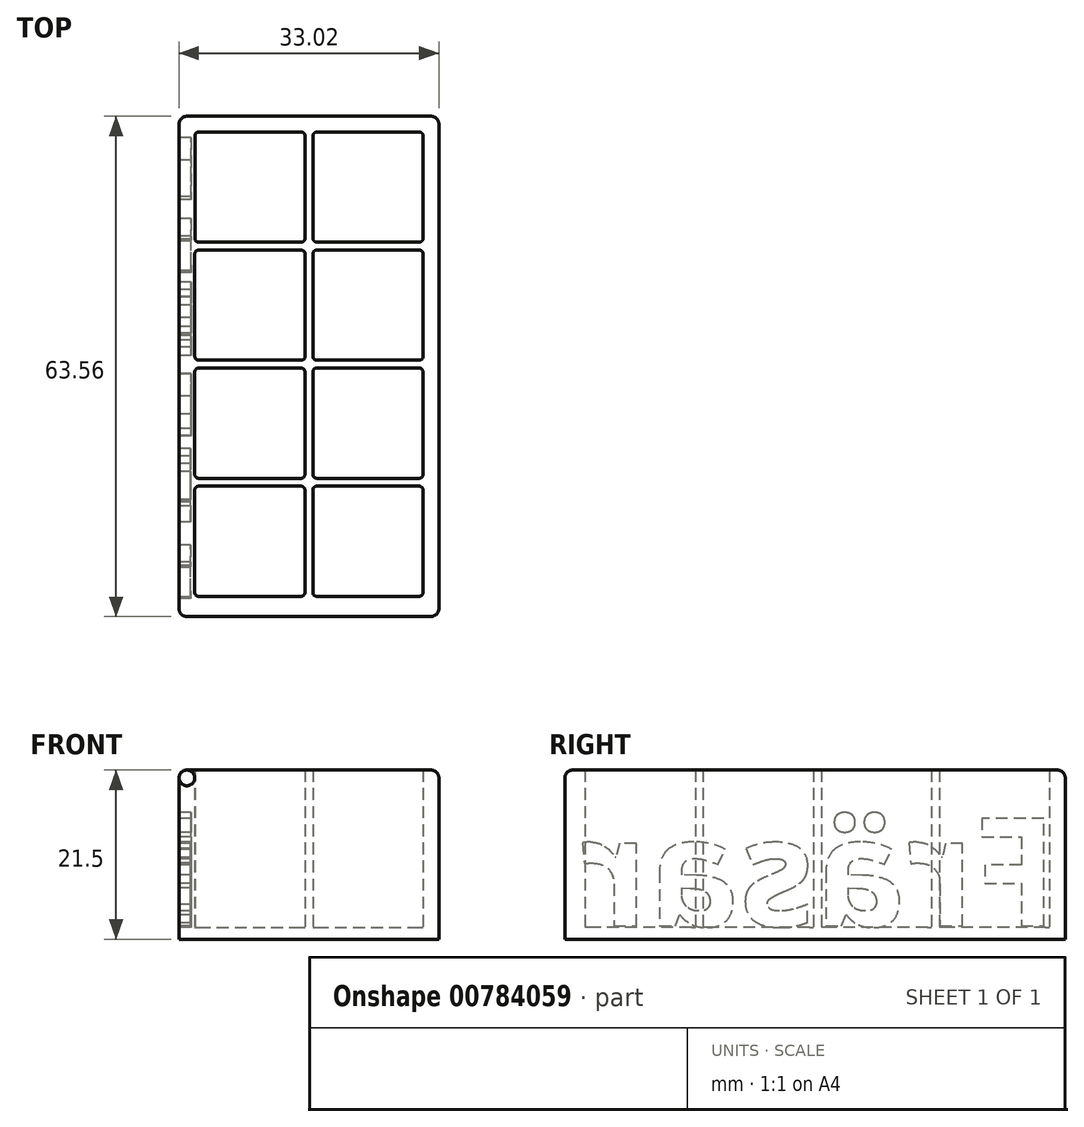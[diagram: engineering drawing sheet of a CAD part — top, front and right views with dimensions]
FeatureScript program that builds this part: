
annotation { "Feature Type Name" : "Feature", "Feature Type Description" : "" }
export const myFeature = defineFeature(function(context is Context, id is Id, definition is map)
    precondition{}
    {
        {
            var Q0;
            Q0=qCreatedBy(makeId("Top.planeOp"),FACE);
            var sketch = newSketch(context, id + "F0", { "sketchPlane" : qUnion([Q0])});
            skLineSegment(sketch, "E0.bottom", {"start": v(-10.2, 14) * mm, "end": v(3.8, 14) * mm});
            skLineSegment(sketch, "E0.top", {"start": v(-10.2, 0) * mm, "end": v(3.8, 0) * mm});
            skLineSegment(sketch, "E0.left", {"start": v(-10.2, 14) * mm, "end": v(-10.2, 0) * mm});
            skLineSegment(sketch, "E0.right", {"start": v(3.8, 14) * mm, "end": v(3.8, 0) * mm});
            skLineSegment(sketch, "E1.0.1.0", {"start": v(-10.2, -1) * mm, "end": v(3.8, -1) * mm});
            skLineSegment(sketch, "E1.0.1.1", {"start": v(-10.2, -1) * mm, "end": v(-10.2, -15) * mm});
            skLineSegment(sketch, "E1.0.1.2", {"start": v(3.8, -1) * mm, "end": v(3.8, -15) * mm});
            skLineSegment(sketch, "E1.0.1.3", {"start": v(-10.2, -15) * mm, "end": v(3.8, -15) * mm});
            skLineSegment(sketch, "E1.0.2.0", {"start": v(-10.2, -16) * mm, "end": v(3.8, -16) * mm});
            skLineSegment(sketch, "E1.0.2.1", {"start": v(-10.2, -16) * mm, "end": v(-10.2, -30) * mm});
            skLineSegment(sketch, "E1.0.2.2", {"start": v(3.8, -16) * mm, "end": v(3.8, -30) * mm});
            skLineSegment(sketch, "E1.0.2.3", {"start": v(-10.2, -30) * mm, "end": v(3.8, -30) * mm});
            skLineSegment(sketch, "E1.0.3.0", {"start": v(-10.2, -31) * mm, "end": v(3.8, -31) * mm});
            skLineSegment(sketch, "E1.0.3.1", {"start": v(-10.2, -31) * mm, "end": v(-10.2, -45) * mm});
            skLineSegment(sketch, "E1.0.3.2", {"start": v(3.8, -31) * mm, "end": v(3.8, -45) * mm});
            skLineSegment(sketch, "E1.0.3.3", {"start": v(-10.2, -45) * mm, "end": v(3.8, -45) * mm});
            skLineSegment(sketch, "E1.1.0.0", {"start": v(4.8, 14) * mm, "end": v(18.8, 14) * mm});
            skLineSegment(sketch, "E1.1.0.1", {"start": v(4.8, 14) * mm, "end": v(4.8, 0) * mm});
            skLineSegment(sketch, "E1.1.0.2", {"start": v(18.8, 14) * mm, "end": v(18.8, 0) * mm});
            skLineSegment(sketch, "E1.1.0.3", {"start": v(4.8, 0) * mm, "end": v(18.8, 0) * mm});
            skLineSegment(sketch, "E1.1.1.0", {"start": v(4.8, -1) * mm, "end": v(18.8, -1) * mm});
            skLineSegment(sketch, "E1.1.1.1", {"start": v(4.8, -1) * mm, "end": v(4.8, -15) * mm});
            skLineSegment(sketch, "E1.1.1.2", {"start": v(18.8, -1) * mm, "end": v(18.8, -15) * mm});
            skLineSegment(sketch, "E1.1.1.3", {"start": v(4.8, -15) * mm, "end": v(18.8, -15) * mm});
            skLineSegment(sketch, "E1.1.2.0", {"start": v(4.8, -16) * mm, "end": v(18.8, -16) * mm});
            skLineSegment(sketch, "E1.1.2.1", {"start": v(4.8, -16) * mm, "end": v(4.8, -30) * mm});
            skLineSegment(sketch, "E1.1.2.2", {"start": v(18.8, -16) * mm, "end": v(18.8, -30) * mm});
            skLineSegment(sketch, "E1.1.2.3", {"start": v(4.8, -30) * mm, "end": v(18.8, -30) * mm});
            skLineSegment(sketch, "E1.1.3.0", {"start": v(4.8, -31) * mm, "end": v(18.8, -31) * mm});
            skLineSegment(sketch, "E1.1.3.1", {"start": v(4.8, -31) * mm, "end": v(4.8, -45) * mm});
            skLineSegment(sketch, "E1.1.3.2", {"start": v(18.8, -31) * mm, "end": v(18.8, -45) * mm});
            skLineSegment(sketch, "E1.1.3.3", {"start": v(4.8, -45) * mm, "end": v(18.8, -45) * mm});
            skLineSegment(sketch, "E1.direction1", {"start": v(-10.2, 14) * mm, "end": v(4.8, 14) * mm, "construction": true});
            skLineSegment(sketch, "E1.direction2", {"start": v(-10.2, 14) * mm, "end": v(-10.2, -1) * mm, "construction": true});
            skPoint(sketch, "E2.bottom.start.orphan", {"position": v(-10.2, -46) * mm});
            skSolve(sketch);
        }
        {
            var Q0;
            Q0=qCreatedBy(makeId("Top.planeOp"),FACE);
            var sketch = newSketch(context, id + "F1", { "sketchPlane" : qUnion([Q0])});
            skLineSegment(sketch, "E3", {"start": v(-10.2, 14) * mm, "end": v(18.8, 14) * mm});
            skLineSegment(sketch, "E4", {"start": v(18.8, 14) * mm, "end": v(18.8, -45.05) * mm});
            skLineSegment(sketch, "E5", {"start": v(18.8, -45.05) * mm, "end": v(-10.2, -45.05) * mm});
            skLineSegment(sketch, "E6", {"start": v(-10.2, -45.05) * mm, "end": v(-10.2, 14) * mm});
            skLineSegment(sketch, "E7.0", {"start": v(20.8, 16) * mm, "end": v(20.8, -47.56) * mm});
            skLineSegment(sketch, "E7.2", {"start": v(20.9, -47.56) * mm, "end": v(-12.2, -47.56) * mm});
            skLineSegment(sketch, "E7.4", {"start": v(-12.2, -47.56) * mm, "end": v(-12.2, 16) * mm});
            skLineSegment(sketch, "E7.5", {"start": v(-12.2, 16) * mm, "end": v(20.8, 16) * mm});
            skSolve(sketch);
        }
        {
            var Q0;
            Q0=makeQuery(id+"F1.imprint","IMPRINT",FACE,{"disambiguationData":[TD([[makeQuery(id+"F1.imprint","IMPRINT",EDGE,{"derivedFrom":sQuery(id+"F1.wireOp",EDGE,"E3")}),1.0]])]});
            var Q1;
            Q1=makeQuery(id+"F1.imprint","IMPRINT",FACE,{"disambiguationData":[TD([[makeQuery(id+"F1.imprint","IMPRINT",EDGE,{"derivedFrom":sQuery(id+"F1.wireOp",EDGE,"E3")}),-1.0]])]});
            extrude(context, id + "F2", {"entities" : qUnion([Q0, Q1]), "depth" : 20 * mm, "offsetDistance" : 25 * mm, "hasSecondDirection" : true, "secondDirectionOppositeDirection" : true, "secondDirectionDepth" : 1.5 * mm});
        }
        {
            var Q0;
            Q0=makeQuery(id+"F0.imprint","IMPRINT",FACE,{"disambiguationData":[TD([[makeQuery(id+"F0.imprint","IMPRINT",EDGE,{"derivedFrom":sQuery(id+"F0.wireOp",EDGE,"E0.bottom")}),-1.0]])]});
            var Q1;
            Q1=makeQuery(id+"F0.imprint","IMPRINT",FACE,{"disambiguationData":[TD([[makeQuery(id+"F0.imprint","IMPRINT",EDGE,{"derivedFrom":sQuery(id+"F0.wireOp",EDGE,"E1.1.0.0")}),-1.0]])]});
            var Q2;
            Q2=makeQuery(id+"F0.imprint","IMPRINT",FACE,{"disambiguationData":[TD([[makeQuery(id+"F0.imprint","IMPRINT",EDGE,{"derivedFrom":sQuery(id+"F0.wireOp",EDGE,"E1.0.1.0")}),-1.0]])]});
            var Q3;
            Q3=makeQuery(id+"F0.imprint","IMPRINT",FACE,{"disambiguationData":[TD([[makeQuery(id+"F0.imprint","IMPRINT",EDGE,{"derivedFrom":sQuery(id+"F0.wireOp",EDGE,"E1.1.1.0")}),-1.0]])]});
            var Q4;
            Q4=makeQuery(id+"F0.imprint","IMPRINT",FACE,{"disambiguationData":[TD([[makeQuery(id+"F0.imprint","IMPRINT",EDGE,{"derivedFrom":sQuery(id+"F0.wireOp",EDGE,"E1.0.2.0")}),-1.0]])]});
            var Q5;
            Q5=makeQuery(id+"F0.imprint","IMPRINT",FACE,{"disambiguationData":[TD([[makeQuery(id+"F0.imprint","IMPRINT",EDGE,{"derivedFrom":sQuery(id+"F0.wireOp",EDGE,"E1.1.2.0")}),-1.0]])]});
            var Q6;
            Q6=makeQuery(id+"F0.imprint","IMPRINT",FACE,{"disambiguationData":[TD([[makeQuery(id+"F0.imprint","IMPRINT",EDGE,{"derivedFrom":sQuery(id+"F0.wireOp",EDGE,"E1.0.3.0")}),-1.0]])]});
            var Q7;
            Q7=makeQuery(id+"F0.imprint","IMPRINT",FACE,{"disambiguationData":[TD([[makeQuery(id+"F0.imprint","IMPRINT",EDGE,{"derivedFrom":sQuery(id+"F0.wireOp",EDGE,"E1.1.3.0")}),-1.0]])]});
            var Q8;
            Q8=makeQuery(id+"F0.imprint","IMPRINT",FACE,{"disambiguationData":[TD([[makeQuery(id+"F0.imprint","IMPRINT",EDGE,{"derivedFrom":sQuery(id+"F0.wireOp",EDGE,"E2.bottom")}),-1.0]])]});
            var Q9;
            Q9=makeQuery(id+"F0.imprint","IMPRINT",FACE,{"disambiguationData":[TD([[makeQuery(id+"F0.imprint","IMPRINT",EDGE,{"derivedFrom":sQuery(id+"F0.wireOp",EDGE,"f9a36279-b497-429b-bdca-f29c6110149f.1.0.0")}),-1.0]])]});
            var Q10;
            Q10=makeQuery(id+"F2.opExtrude","CAP_FACE",FACE,{"disambiguationData":[OSD([sQuery(id+"F1.wireOp",EDGE,"E7.0"),sQuery(id+"F1.wireOp",EDGE,"E7.1"),sQuery(id+"F1.wireOp",EDGE,"E7.2"),sQuery(id+"F1.wireOp",EDGE,"E7.3"),sQuery(id+"F1.wireOp",EDGE,"E7.4"),sQuery(id+"F1.wireOp",EDGE,"E7.5")])],"isStart":false});
            extrude(context, id + "F3", {"entities" : qUnion([Q0, Q1, Q2, Q3, Q4, Q5, Q6, Q7, Q8, Q9]), "operationType" : NewBodyOperationType.REMOVE, "endBound" : BoundingType.UP_TO_SURFACE, "depth" : 25 * mm, "endBoundEntityFace" : qUnion([Q10]), "offsetDistance" : 25 * mm});
        }
        {
            var Q0;
            Q0=makeQuery(id+"F2.opExtrude","CAP_EDGE",EDGE,{"disambiguationData":[OSD([sQuery(id+"F1.wireOp",EDGE,"E7.0")])],"isStart":false});
            var Q1;
            Q1=makeQuery(id+"F2.opExtrude","CAP_EDGE",EDGE,{"disambiguationData":[OSD([sQuery(id+"F1.wireOp",EDGE,"E7.3")])],"isStart":false});
            var Q2;
            Q2=makeQuery(id+"F2.opExtrude","CAP_EDGE",EDGE,{"disambiguationData":[OSD([sQuery(id+"F1.wireOp",EDGE,"E7.1")])],"isStart":false});
            var Q3;
            Q3=makeQuery(id+"F2.opExtrude","CAP_EDGE",EDGE,{"disambiguationData":[OSD([sQuery(id+"F1.wireOp",EDGE,"E7.4")])],"isStart":false});
            var Q4;
            Q4=makeQuery(id+"F2.opExtrude","SWEPT_EDGE",EDGE,{"disambiguationData":[OSD([sQuery(id+"F1.wireOp",EDGE,"E7.1"),sQuery(id+"F1.wireOp",EDGE,"E7.2")])]});
            var Q5;
            Q5=makeQuery(id+"F2.opExtrude","SWEPT_EDGE",EDGE,{"disambiguationData":[OSD([sQuery(id+"F1.wireOp",EDGE,"E7.1"),sQuery(id+"F1.wireOp",EDGE,"E7.3")])]});
            var Q6;
            Q6=makeQuery(id+"F2.opExtrude","SWEPT_EDGE",EDGE,{"disambiguationData":[OSD([sQuery(id+"F1.wireOp",EDGE,"E7.0"),sQuery(id+"F1.wireOp",EDGE,"E7.5")])]});
            var Q7;
            Q7=makeQuery(id+"F2.opExtrude","CAP_EDGE",EDGE,{"disambiguationData":[OSD([sQuery(id+"F1.wireOp",EDGE,"E7.5")])],"isStart":false});
            var Q8;
            Q8=makeQuery(id+"F2.opExtrude","SWEPT_EDGE",EDGE,{"disambiguationData":[OSD([sQuery(id+"F1.wireOp",EDGE,"E7.4"),sQuery(id+"F1.wireOp",EDGE,"E7.5")])]});
            var Q9;
            Q9=makeQuery(id+"F2.opExtrude","SWEPT_EDGE",EDGE,{"disambiguationData":[OSD([sQuery(id+"F1.wireOp",EDGE,"E7.0"),sQuery(id+"F1.wireOp",EDGE,"E7.3")])]});
            var Q10;
            Q10=makeQuery(id+"F2.opExtrude","CAP_EDGE",EDGE,{"disambiguationData":[OSD([sQuery(id+"F1.wireOp",EDGE,"E7.2")])],"isStart":false});
            var Q11;
            Q11=makeQuery(id+"F2.opExtrude","SWEPT_EDGE",EDGE,{"disambiguationData":[OSD([sQuery(id+"F1.wireOp",EDGE,"E7.2"),sQuery(id+"F1.wireOp",EDGE,"E7.4")])]});
            fillet(context, id + "F4", {"entities" : qUnion([Q0, Q1, Q2, Q3, Q4, Q5, Q6, Q7, Q8, Q9, Q10, Q11]), "radius" : 1 * mm, "allowEdgeOverflow" : false});
        }
        {
            var Q0;
            Q0=makeQuery(id+"F3.boolean.opBoolean","COPY",EDGE,{"derivedFrom":makeQuery(id+"F3.opExtrude","SWEPT_EDGE",EDGE,{"disambiguationData":[OSD([sQuery(id+"F0.wireOp",EDGE,"E1.1.0.0"),sQuery(id+"F0.wireOp",EDGE,"E1.1.0.2")])]})});
            var Q1;
            Q1=makeQuery(id+"F3.boolean.opBoolean","COPY",EDGE,{"derivedFrom":makeQuery(id+"F3.opExtrude","SWEPT_EDGE",EDGE,{"disambiguationData":[OSD([sQuery(id+"F0.wireOp",EDGE,"E1.1.1.0"),sQuery(id+"F0.wireOp",EDGE,"E1.1.1.2")])]})});
            var Q2;
            Q2=makeQuery(id+"F3.boolean.opBoolean","COPY",EDGE,{"derivedFrom":makeQuery(id+"F3.opExtrude","SWEPT_EDGE",EDGE,{"disambiguationData":[OSD([sQuery(id+"F0.wireOp",EDGE,"E1.1.2.0"),sQuery(id+"F0.wireOp",EDGE,"E1.1.2.2")])]})});
            var Q3;
            Q3=makeQuery(id+"F3.boolean.opBoolean","COPY",EDGE,{"derivedFrom":makeQuery(id+"F3.opExtrude","SWEPT_EDGE",EDGE,{"disambiguationData":[OSD([sQuery(id+"F0.wireOp",EDGE,"E1.1.3.0"),sQuery(id+"F0.wireOp",EDGE,"E1.1.3.2")])]})});
            var Q4;
            Q4=makeQuery(id+"F3.boolean.opBoolean","COPY",EDGE,{"derivedFrom":makeQuery(id+"F3.opExtrude","SWEPT_EDGE",EDGE,{"disambiguationData":[OSD([sQuery(id+"F0.wireOp",EDGE,"f9a36279-b497-429b-bdca-f29c6110149f.1.0.0"),sQuery(id+"F0.wireOp",EDGE,"f9a36279-b497-429b-bdca-f29c6110149f.1.0.1")])]})});
            var Q5;
            Q5=makeQuery(id+"F3.boolean.opBoolean","COPY",EDGE,{"derivedFrom":makeQuery(id+"F3.opExtrude","SWEPT_EDGE",EDGE,{"disambiguationData":[OSD([sQuery(id+"F0.wireOp",EDGE,"E0.bottom"),sQuery(id+"F0.wireOp",EDGE,"E0.right")])]})});
            var Q6;
            Q6=makeQuery(id+"F3.boolean.opBoolean","COPY",EDGE,{"derivedFrom":makeQuery(id+"F3.opExtrude","SWEPT_EDGE",EDGE,{"disambiguationData":[OSD([sQuery(id+"F0.wireOp",EDGE,"E1.0.1.0"),sQuery(id+"F0.wireOp",EDGE,"E1.0.1.2")])]})});
            var Q7;
            Q7=makeQuery(id+"F3.boolean.opBoolean","COPY",EDGE,{"derivedFrom":makeQuery(id+"F3.opExtrude","SWEPT_EDGE",EDGE,{"disambiguationData":[OSD([sQuery(id+"F0.wireOp",EDGE,"E1.0.2.0"),sQuery(id+"F0.wireOp",EDGE,"E1.0.2.2")])]})});
            var Q8;
            Q8=makeQuery(id+"F3.boolean.opBoolean","COPY",EDGE,{"derivedFrom":makeQuery(id+"F3.opExtrude","SWEPT_EDGE",EDGE,{"disambiguationData":[OSD([sQuery(id+"F0.wireOp",EDGE,"E1.0.3.0"),sQuery(id+"F0.wireOp",EDGE,"E1.0.3.2")])]})});
            var Q9;
            Q9=makeQuery(id+"F3.boolean.opBoolean","COPY",EDGE,{"derivedFrom":makeQuery(id+"F3.opExtrude","SWEPT_EDGE",EDGE,{"disambiguationData":[OSD([sQuery(id+"F0.wireOp",EDGE,"E2.bottom"),sQuery(id+"F0.wireOp",EDGE,"E2.right")])]})});
            var Q10;
            Q10=makeQuery(id+"F3.boolean.opBoolean","COPY",EDGE,{"derivedFrom":makeQuery(id+"F3.opExtrude","SWEPT_EDGE",EDGE,{"disambiguationData":[OSD([sQuery(id+"F0.wireOp",EDGE,"E1.1.0.2"),sQuery(id+"F0.wireOp",EDGE,"E1.1.0.3")])]})});
            var Q11;
            Q11=makeQuery(id+"F3.boolean.opBoolean","COPY",EDGE,{"derivedFrom":makeQuery(id+"F3.opExtrude","SWEPT_EDGE",EDGE,{"disambiguationData":[OSD([sQuery(id+"F0.wireOp",EDGE,"E1.1.1.2"),sQuery(id+"F0.wireOp",EDGE,"E1.1.1.3")])]})});
            var Q12;
            Q12=makeQuery(id+"F3.boolean.opBoolean","COPY",EDGE,{"derivedFrom":makeQuery(id+"F3.opExtrude","SWEPT_EDGE",EDGE,{"disambiguationData":[OSD([sQuery(id+"F0.wireOp",EDGE,"E1.1.2.2"),sQuery(id+"F0.wireOp",EDGE,"E1.1.2.3")])]})});
            var Q13;
            Q13=makeQuery(id+"F3.boolean.opBoolean","COPY",EDGE,{"derivedFrom":makeQuery(id+"F3.opExtrude","SWEPT_EDGE",EDGE,{"disambiguationData":[OSD([sQuery(id+"F0.wireOp",EDGE,"E1.1.3.2"),sQuery(id+"F0.wireOp",EDGE,"E1.1.3.3")])]})});
            var Q14;
            Q14=makeQuery(id+"F3.boolean.opBoolean","COPY",EDGE,{"derivedFrom":makeQuery(id+"F3.opExtrude","SWEPT_EDGE",EDGE,{"disambiguationData":[OSD([sQuery(id+"F0.wireOp",EDGE,"f9a36279-b497-429b-bdca-f29c6110149f.1.0.0"),sQuery(id+"F0.wireOp",EDGE,"f9a36279-b497-429b-bdca-f29c6110149f.1.0.3")])]})});
            var Q15;
            Q15=makeQuery(id+"F3.boolean.opBoolean","COPY",EDGE,{"derivedFrom":makeQuery(id+"F3.opExtrude","SWEPT_EDGE",EDGE,{"disambiguationData":[OSD([sQuery(id+"F0.wireOp",EDGE,"E2.top"),sQuery(id+"F0.wireOp",EDGE,"E2.right")])]})});
            var Q16;
            Q16=makeQuery(id+"F3.boolean.opBoolean","COPY",EDGE,{"derivedFrom":makeQuery(id+"F3.opExtrude","SWEPT_EDGE",EDGE,{"disambiguationData":[OSD([sQuery(id+"F0.wireOp",EDGE,"E1.0.3.2"),sQuery(id+"F0.wireOp",EDGE,"E1.0.3.3")])]})});
            var Q17;
            Q17=makeQuery(id+"F3.boolean.opBoolean","COPY",EDGE,{"derivedFrom":makeQuery(id+"F3.opExtrude","SWEPT_EDGE",EDGE,{"disambiguationData":[OSD([sQuery(id+"F0.wireOp",EDGE,"E1.0.2.2"),sQuery(id+"F0.wireOp",EDGE,"E1.0.2.3")])]})});
            var Q18;
            Q18=makeQuery(id+"F3.boolean.opBoolean","COPY",EDGE,{"derivedFrom":makeQuery(id+"F3.opExtrude","SWEPT_EDGE",EDGE,{"disambiguationData":[OSD([sQuery(id+"F0.wireOp",EDGE,"E1.0.1.2"),sQuery(id+"F0.wireOp",EDGE,"E1.0.1.3")])]})});
            var Q19;
            Q19=makeQuery(id+"F3.boolean.opBoolean","COPY",EDGE,{"derivedFrom":makeQuery(id+"F3.opExtrude","SWEPT_EDGE",EDGE,{"disambiguationData":[OSD([sQuery(id+"F0.wireOp",EDGE,"E0.top"),sQuery(id+"F0.wireOp",EDGE,"E0.right")])]})});
            var Q20;
            Q20=makeQuery(id+"F3.boolean.opBoolean","COPY",EDGE,{"derivedFrom":makeQuery(id+"F3.opExtrude","SWEPT_EDGE",EDGE,{"disambiguationData":[OSD([sQuery(id+"F0.wireOp",EDGE,"E0.bottom"),sQuery(id+"F0.wireOp",EDGE,"E0.left")])]})});
            var Q21;
            Q21=makeQuery(id+"F3.boolean.opBoolean","COPY",EDGE,{"derivedFrom":makeQuery(id+"F3.opExtrude","SWEPT_EDGE",EDGE,{"disambiguationData":[OSD([sQuery(id+"F0.wireOp",EDGE,"E1.0.1.0"),sQuery(id+"F0.wireOp",EDGE,"E1.0.1.1")])]})});
            var Q22;
            Q22=makeQuery(id+"F3.boolean.opBoolean","COPY",EDGE,{"derivedFrom":makeQuery(id+"F3.opExtrude","SWEPT_EDGE",EDGE,{"disambiguationData":[OSD([sQuery(id+"F0.wireOp",EDGE,"E1.0.2.0"),sQuery(id+"F0.wireOp",EDGE,"E1.0.2.1")])]})});
            var Q23;
            Q23=makeQuery(id+"F3.boolean.opBoolean","COPY",EDGE,{"derivedFrom":makeQuery(id+"F3.opExtrude","SWEPT_EDGE",EDGE,{"disambiguationData":[OSD([sQuery(id+"F0.wireOp",EDGE,"E1.0.3.0"),sQuery(id+"F0.wireOp",EDGE,"E1.0.3.1")])]})});
            var Q24;
            Q24=makeQuery(id+"F3.boolean.opBoolean","COPY",EDGE,{"derivedFrom":makeQuery(id+"F3.opExtrude","SWEPT_EDGE",EDGE,{"disambiguationData":[OSD([sQuery(id+"F0.wireOp",EDGE,"E2.bottom"),sQuery(id+"F0.wireOp",EDGE,"E2.left")])]})});
            var Q25;
            Q25=makeQuery(id+"F3.boolean.opBoolean","COPY",EDGE,{"derivedFrom":makeQuery(id+"F3.opExtrude","SWEPT_EDGE",EDGE,{"disambiguationData":[OSD([sQuery(id+"F0.wireOp",EDGE,"E2.top"),sQuery(id+"F0.wireOp",EDGE,"E2.left")])]})});
            var Q26;
            Q26=makeQuery(id+"F3.boolean.opBoolean","COPY",EDGE,{"derivedFrom":makeQuery(id+"F3.opExtrude","SWEPT_EDGE",EDGE,{"disambiguationData":[OSD([sQuery(id+"F0.wireOp",EDGE,"E1.0.1.1"),sQuery(id+"F0.wireOp",EDGE,"E1.0.1.3")])]})});
            var Q27;
            Q27=makeQuery(id+"F3.boolean.opBoolean","COPY",EDGE,{"derivedFrom":makeQuery(id+"F3.opExtrude","SWEPT_EDGE",EDGE,{"disambiguationData":[OSD([sQuery(id+"F0.wireOp",EDGE,"E0.top"),sQuery(id+"F0.wireOp",EDGE,"E0.left")])]})});
            var Q28;
            Q28=makeQuery(id+"F3.boolean.opBoolean","COPY",EDGE,{"derivedFrom":makeQuery(id+"F3.opExtrude","SWEPT_EDGE",EDGE,{"disambiguationData":[OSD([sQuery(id+"F0.wireOp",EDGE,"E1.1.0.0"),sQuery(id+"F0.wireOp",EDGE,"E1.1.0.1")])]})});
            var Q29;
            Q29=makeQuery(id+"F3.boolean.opBoolean","COPY",EDGE,{"derivedFrom":makeQuery(id+"F3.opExtrude","SWEPT_EDGE",EDGE,{"disambiguationData":[OSD([sQuery(id+"F0.wireOp",EDGE,"E1.1.0.1"),sQuery(id+"F0.wireOp",EDGE,"E1.1.0.3")])]})});
            var Q30;
            Q30=makeQuery(id+"F3.boolean.opBoolean","COPY",EDGE,{"derivedFrom":makeQuery(id+"F3.opExtrude","SWEPT_EDGE",EDGE,{"disambiguationData":[OSD([sQuery(id+"F0.wireOp",EDGE,"E1.1.1.0"),sQuery(id+"F0.wireOp",EDGE,"E1.1.1.1")])]})});
            var Q31;
            Q31=makeQuery(id+"F3.boolean.opBoolean","COPY",EDGE,{"derivedFrom":makeQuery(id+"F3.opExtrude","SWEPT_EDGE",EDGE,{"disambiguationData":[OSD([sQuery(id+"F0.wireOp",EDGE,"E1.1.1.1"),sQuery(id+"F0.wireOp",EDGE,"E1.1.1.3")])]})});
            var Q32;
            Q32=makeQuery(id+"F3.boolean.opBoolean","COPY",EDGE,{"derivedFrom":makeQuery(id+"F3.opExtrude","SWEPT_EDGE",EDGE,{"disambiguationData":[OSD([sQuery(id+"F0.wireOp",EDGE,"E1.1.2.0"),sQuery(id+"F0.wireOp",EDGE,"E1.1.2.1")])]})});
            var Q33;
            Q33=makeQuery(id+"F3.boolean.opBoolean","COPY",EDGE,{"derivedFrom":makeQuery(id+"F3.opExtrude","SWEPT_EDGE",EDGE,{"disambiguationData":[OSD([sQuery(id+"F0.wireOp",EDGE,"E1.0.2.1"),sQuery(id+"F0.wireOp",EDGE,"E1.0.2.3")])]})});
            var Q34;
            Q34=makeQuery(id+"F3.boolean.opBoolean","COPY",EDGE,{"derivedFrom":makeQuery(id+"F3.opExtrude","SWEPT_EDGE",EDGE,{"disambiguationData":[OSD([sQuery(id+"F0.wireOp",EDGE,"E1.1.2.1"),sQuery(id+"F0.wireOp",EDGE,"E1.1.2.3")])]})});
            var Q35;
            Q35=makeQuery(id+"F3.boolean.opBoolean","COPY",EDGE,{"derivedFrom":makeQuery(id+"F3.opExtrude","SWEPT_EDGE",EDGE,{"disambiguationData":[OSD([sQuery(id+"F0.wireOp",EDGE,"E1.1.3.0"),sQuery(id+"F0.wireOp",EDGE,"E1.1.3.1")])]})});
            var Q36;
            Q36=makeQuery(id+"F3.boolean.opBoolean","COPY",EDGE,{"derivedFrom":makeQuery(id+"F3.opExtrude","SWEPT_EDGE",EDGE,{"disambiguationData":[OSD([sQuery(id+"F0.wireOp",EDGE,"E1.1.3.1"),sQuery(id+"F0.wireOp",EDGE,"E1.1.3.3")])]})});
            var Q37;
            Q37=makeQuery(id+"F3.boolean.opBoolean","COPY",EDGE,{"derivedFrom":makeQuery(id+"F3.opExtrude","SWEPT_EDGE",EDGE,{"disambiguationData":[OSD([sQuery(id+"F0.wireOp",EDGE,"E1.0.3.1"),sQuery(id+"F0.wireOp",EDGE,"E1.0.3.3")])]})});
            var Q38;
            Q38=makeQuery(id+"F3.boolean.opBoolean","COPY",EDGE,{"derivedFrom":makeQuery(id+"F3.opExtrude","SWEPT_EDGE",EDGE,{"disambiguationData":[OSD([sQuery(id+"F0.wireOp",EDGE,"f9a36279-b497-429b-bdca-f29c6110149f.1.0.1"),sQuery(id+"F0.wireOp",EDGE,"f9a36279-b497-429b-bdca-f29c6110149f.1.0.2")])]})});
            var Q39;
            Q39=makeQuery(id+"F3.boolean.opBoolean","COPY",EDGE,{"derivedFrom":makeQuery(id+"F3.opExtrude","SWEPT_EDGE",EDGE,{"disambiguationData":[OSD([sQuery(id+"F0.wireOp",EDGE,"f9a36279-b497-429b-bdca-f29c6110149f.1.0.2"),sQuery(id+"F0.wireOp",EDGE,"f9a36279-b497-429b-bdca-f29c6110149f.1.0.3")])]})});
            fillet(context, id + "F5", {"entities" : qUnion([Q0, Q1, Q2, Q3, Q4, Q5, Q6, Q7, Q8, Q9, Q10, Q11, Q12, Q13, Q14, Q15, Q16, Q17, Q18, Q19, Q20, Q21, Q22, Q23, Q24, Q25, Q26, Q27, Q28, Q29, Q30, Q31, Q32, Q33, Q34, Q35, Q36, Q37, Q38, Q39]), "radius" : 0.5 * mm, "tangentPropagation" : true, "allowEdgeOverflow" : false});
        }
        {
            var Q0;
            Q0=makeQuery(id+"F2.opExtrude","SWEPT_FACE",FACE,{"disambiguationData":[OSD([sQuery(id+"F1.wireOp",EDGE,"E7.4")])]});
            var sketch = newSketch(context, id + "F6", { "sketchPlane" : qUnion([Q0])});
            skText(sketch, "E8", { "text": "Fräsar", "fontName": "OpenSans-Bold.ttf"});
            const initialGuessF6  = {"E8": [-0.015, 0.00018, 1, 0, 0.01382]};
            skSetInitialGuess(sketch, initialGuessF6);
            skSolve(sketch);
        }
        {
            var Q0;
            Q0=qSketchRegion(id+"F6",true);
            extrude(context, id + "F7", {"entities" : qUnion([Q0]), "operationType" : NewBodyOperationType.REMOVE, "oppositeDirection" : true, "depth" : 1.5 * mm, "offsetDistance" : 25 * mm});
        }
    });
